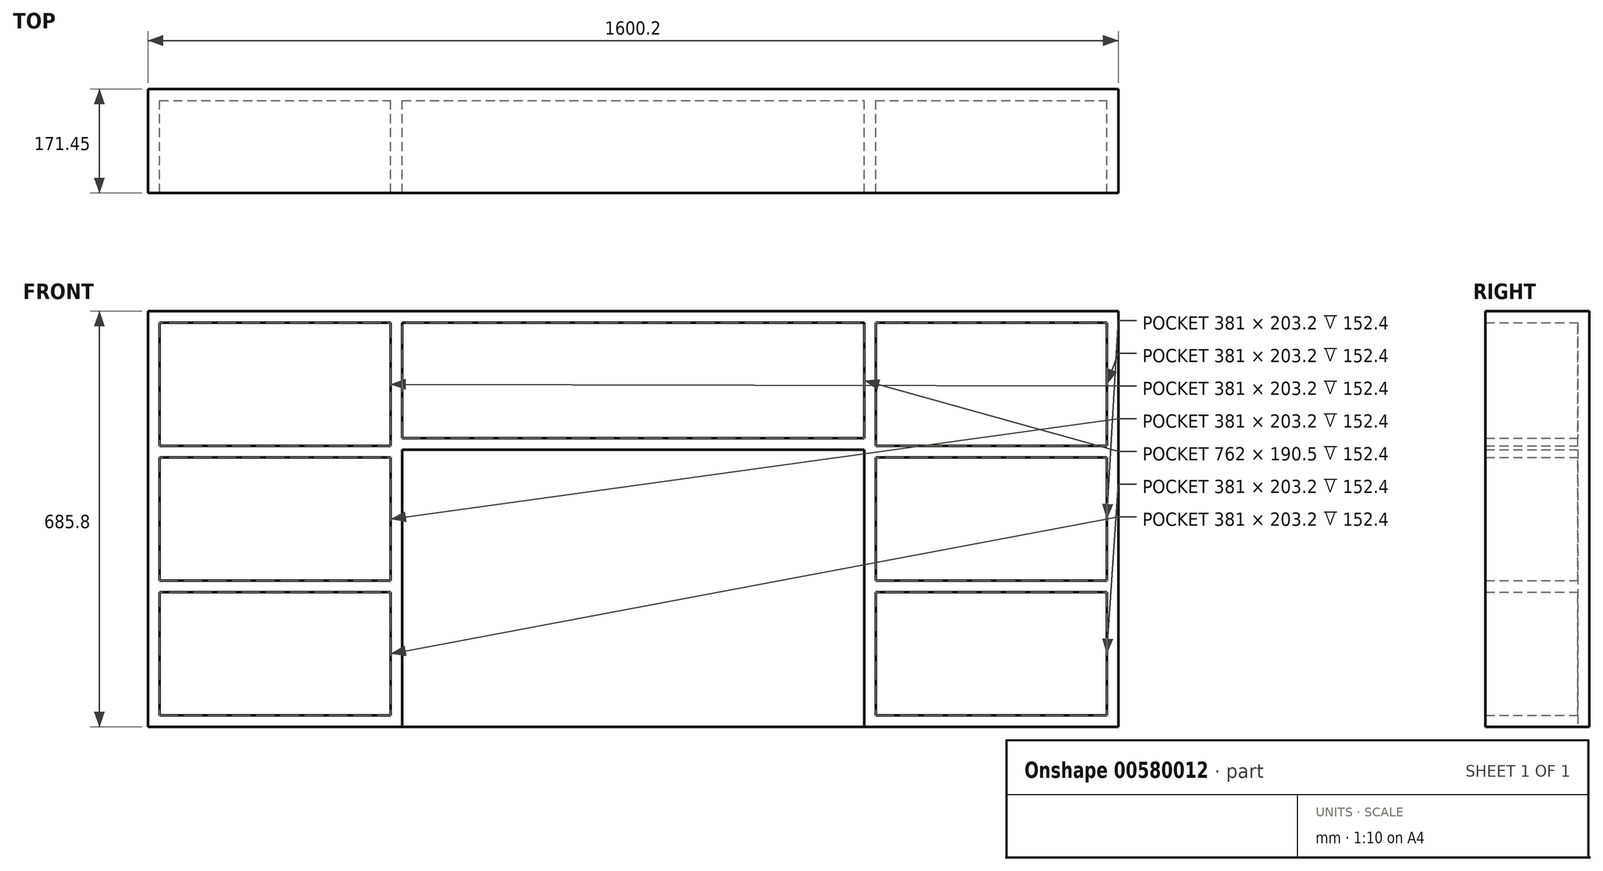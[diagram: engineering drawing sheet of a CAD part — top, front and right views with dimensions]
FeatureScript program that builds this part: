
annotation { "Feature Type Name" : "Feature", "Feature Type Description" : "" }
export const myFeature = defineFeature(function(context is Context, id is Id, definition is map)
    precondition{}
    {
        {
            var Q0;
            Q0=qCreatedBy(makeId("Front.planeOp"),FACE);
            var sketch = newSketch(context, id + "F0", { "sketchPlane" : qUnion([Q0])});
            skLineSegment(sketch, "E0.bottom", {"start": v(0, 0) * mm, "end": v(1600.2, 0) * mm});
            skLineSegment(sketch, "E0.top", {"start": v(0, 685.8) * mm, "end": v(1600.2, 685.8) * mm});
            skLineSegment(sketch, "E0.left", {"start": v(0, 0) * mm, "end": v(0, 685.8) * mm});
            skLineSegment(sketch, "E0.right", {"start": v(1600.2, 0) * mm, "end": v(1600.2, 685.8) * mm});
            skSolve(sketch);
        }
        {
            var Q0;
            Q0=makeQuery(id+"F0.imprint","IMPRINT",FACE,{"disambiguationData":[TD([[makeQuery(id+"F0.imprint","IMPRINT",EDGE,{"derivedFrom":sQuery(id+"F0.wireOp",EDGE,"E0.bottom")}),1.0]])]});
            extrude(context, id + "F1", {"entities" : qUnion([Q0]), "depth" : 19.05 * mm, "offsetDistance" : 25.4 * mm});
        }
        {
            var Q0;
            Q0=makeQuery(id+"F1.opExtrude","CAP_FACE",FACE,{"disambiguationData":[OSD([sQuery(id+"F0.wireOp",EDGE,"E0.bottom"),sQuery(id+"F0.wireOp",EDGE,"E0.top"),sQuery(id+"F0.wireOp",EDGE,"E0.left"),sQuery(id+"F0.wireOp",EDGE,"E0.right")])],"isStart":false});
            var sketch = newSketch(context, id + "F2", { "sketchPlane" : qUnion([Q0])});
            skLineSegment(sketch, "E1", {"start": v(0, 0) * mm, "end": v(19.05, 0) * mm});
            skLineSegment(sketch, "E2", {"start": v(19.05, 0) * mm, "end": v(19.05, 666.75) * mm});
            skLineSegment(sketch, "E3", {"start": v(19.05, 666.75) * mm, "end": v(1581.15, 666.75) * mm});
            skLineSegment(sketch, "E4", {"start": v(1581.15, 666.75) * mm, "end": v(1581.15, 0) * mm});
            skLineSegment(sketch, "E5", {"start": v(1581.15, 0) * mm, "end": v(1600.2, 0) * mm});
            skLineSegment(sketch, "E6", {"start": v(1600.2, 0) * mm, "end": v(1600.2, 685.8) * mm});
            skLineSegment(sketch, "E7", {"start": v(1600.2, 685.8) * mm, "end": v(0, 685.8) * mm});
            skLineSegment(sketch, "E8", {"start": v(0, 685.8) * mm, "end": v(0, 0) * mm});
            skSolve(sketch);
        }
        {
            var Q0;
            Q0=makeQuery(id+"F2.imprint","IMPRINT",FACE,{"disambiguationData":[TD([[makeQuery(id+"F2.imprint","IMPRINT",EDGE,{"derivedFrom":sQuery(id+"F2.wireOp",EDGE,"E1")}),1.0]])]});
            extrude(context, id + "F3", {"entities" : qUnion([Q0]), "operationType" : NewBodyOperationType.ADD, "depth" : 152.4 * mm, "offsetDistance" : 25.4 * mm});
        }
        {
            var Q0;
            Q0=makeQuery(id+"F1.opExtrude","CAP_FACE",FACE,{"disambiguationData":[OSD([sQuery(id+"F0.wireOp",EDGE,"E0.bottom"),sQuery(id+"F0.wireOp",EDGE,"E0.top"),sQuery(id+"F0.wireOp",EDGE,"E0.left"),sQuery(id+"F0.wireOp",EDGE,"E0.right")])],"isStart":false});
            var sketch = newSketch(context, id + "F4", { "sketchPlane" : qUnion([Q0])});
            skLineSegment(sketch, "E9", {"start": v(419.1, 666.75) * mm, "end": v(419.1, 0) * mm});
            skLineSegment(sketch, "E10", {"start": v(419.1, 0) * mm, "end": v(19.05, 0) * mm});
            skLineSegment(sketch, "E11", {"start": v(19.05, 0) * mm, "end": v(19.05, 19.05) * mm});
            skLineSegment(sketch, "E12", {"start": v(19.05, 19.05) * mm, "end": v(400.05, 19.05) * mm});
            skLineSegment(sketch, "E13", {"start": v(400.05, 19.05) * mm, "end": v(400.05, 666.75) * mm});
            skLineSegment(sketch, "E14", {"start": v(400.05, 666.75) * mm, "end": v(419.1, 666.75) * mm});
            skLineSegment(sketch, "E15", {"start": v(800.1, 666.75) * mm, "end": v(800.1, 413.93) * mm, "construction": true});
            skLineSegment(sketch, "E16.MirrorCS", {"start": v(1181.1, 666.75) * mm, "end": v(1181.1, 0) * mm});
            skLineSegment(sketch, "E17.MirrorCS", {"start": v(1200.15, 19.05) * mm, "end": v(1200.15, 666.75) * mm});
            skLineSegment(sketch, "E18.MirrorCS", {"start": v(1581.15, 19.05) * mm, "end": v(1200.15, 19.05) * mm});
            skLineSegment(sketch, "E19.MirrorCS", {"start": v(1181.1, 0) * mm, "end": v(1581.15, 0) * mm});
            skSolve(sketch);
        }
        {
            var Q0;
            Q0=makeQuery(id+"F4.imprint","IMPRINT",FACE,{"disambiguationData":[TD([[makeQuery(id+"F4.imprint","IMPRINT",EDGE,{"derivedFrom":sQuery(id+"F4.wireOp",EDGE,"E9")}),-1.0]])]});
            var Q1;
            {var subQ3=sQuery(id+"F4.wireOp",EDGE,"E16.MirrorCS");Q1=makeQuery(id+"F4.imprint","IMPRINT",FACE,{"disambiguationData":[TD([[makeQuery(id+"F4.imprint","IMPRINT",EDGE,{"derivedFrom":subQ3}),1.0]])]});}
            extrude(context, id + "F5", {"entities" : qUnion([Q0, Q1]), "operationType" : NewBodyOperationType.ADD, "depth" : 152.4 * mm, "offsetDistance" : 25.4 * mm});
        }
        {
            var Q0;
            {var subQ0=sQuery(id+"F0.wireOp",EDGE,"E0.bottom");Q0=makeQuery(id+"F5.boolean.opBoolean","SPLIT",FACE,{"disambiguationData":[TD([makeQuery(id+"F1.opExtrude","SWEPT_FACE",FACE,{"disambiguationData":[OSD([subQ0])]})])],"derivedFrom":makeQuery(id+"F1.opExtrude","CAP_FACE",FACE,{"disambiguationData":[OSD([subQ0,sQuery(id+"F0.wireOp",EDGE,"E0.top"),sQuery(id+"F0.wireOp",EDGE,"E0.left"),sQuery(id+"F0.wireOp",EDGE,"E0.right")])],"isStart":false})});}
            var sketch = newSketch(context, id + "F6", { "sketchPlane" : qUnion([Q0])});
            skLineSegment(sketch, "E20.bottom", {"start": v(419.1, 476.25) * mm, "end": v(1181.1, 476.25) * mm});
            skLineSegment(sketch, "E20.top", {"start": v(419.1, 457.2) * mm, "end": v(1181.1, 457.2) * mm});
            skLineSegment(sketch, "E20.left", {"start": v(419.1, 476.25) * mm, "end": v(419.1, 457.2) * mm});
            skLineSegment(sketch, "E20.right", {"start": v(1181.1, 476.25) * mm, "end": v(1181.1, 457.2) * mm});
            skSolve(sketch);
        }
        {
            var Q0;
            Q0=makeQuery(id+"F6.imprint","IMPRINT",FACE,{"disambiguationData":[TD([[makeQuery(id+"F6.imprint","IMPRINT",EDGE,{"derivedFrom":sQuery(id+"F6.wireOp",EDGE,"E20.bottom")}),-1.0]])]});
            extrude(context, id + "F7", {"entities" : qUnion([Q0]), "operationType" : NewBodyOperationType.ADD, "depth" : 152.4 * mm, "offsetDistance" : 25.4 * mm});
        }
        {
            var Q0;
            Q0=makeQuery(id+"F5.boolean.opBoolean","SPLIT",FACE,{"disambiguationData":[TD([makeQuery(id+"F3.opExtrude","SWEPT_FACE",FACE,{"disambiguationData":[OSD([sQuery(id+"F2.wireOp",EDGE,"E2")])]})])],"derivedFrom":makeQuery(id+"F1.opExtrude","CAP_FACE",FACE,{"disambiguationData":[OSD([sQuery(id+"F0.wireOp",EDGE,"E0.bottom"),sQuery(id+"F0.wireOp",EDGE,"E0.top"),sQuery(id+"F0.wireOp",EDGE,"E0.left"),sQuery(id+"F0.wireOp",EDGE,"E0.right")])],"isStart":false})});
            var sketch = newSketch(context, id + "F8", { "sketchPlane" : qUnion([Q0])});
            skLineSegment(sketch, "E21.bottom", {"start": v(19.05, 241.3) * mm, "end": v(400.05, 241.3) * mm});
            skLineSegment(sketch, "E21.top", {"start": v(19.05, 222.25) * mm, "end": v(400.05, 222.25) * mm});
            skLineSegment(sketch, "E21.left", {"start": v(19.05, 241.3) * mm, "end": v(19.05, 222.25) * mm});
            skLineSegment(sketch, "E21.right", {"start": v(400.05, 241.3) * mm, "end": v(400.05, 222.25) * mm});
            skLineSegment(sketch, "E22.bottom", {"start": v(19.05, 463.55) * mm, "end": v(400.05, 463.55) * mm});
            skLineSegment(sketch, "E22.top", {"start": v(19.05, 444.5) * mm, "end": v(400.05, 444.5) * mm});
            skLineSegment(sketch, "E22.left", {"start": v(19.05, 463.55) * mm, "end": v(19.05, 444.5) * mm});
            skLineSegment(sketch, "E22.right", {"start": v(400.05, 463.55) * mm, "end": v(400.05, 444.5) * mm});
            skSolve(sketch);
        }
        {
            var Q0;
            Q0=makeQuery(id+"F8.imprint","IMPRINT",FACE,{"disambiguationData":[TD([[makeQuery(id+"F8.imprint","IMPRINT",EDGE,{"derivedFrom":sQuery(id+"F8.wireOp",EDGE,"E22.bottom")}),-1.0]])]});
            var Q1;
            Q1=makeQuery(id+"F8.imprint","IMPRINT",FACE,{"disambiguationData":[TD([[makeQuery(id+"F8.imprint","IMPRINT",EDGE,{"derivedFrom":sQuery(id+"F8.wireOp",EDGE,"E21.bottom")}),-1.0]])]});
            extrude(context, id + "F9", {"entities" : qUnion([Q0, Q1]), "operationType" : NewBodyOperationType.ADD, "depth" : 152.4 * mm, "offsetDistance" : 25.4 * mm});
        }
        {
            var Q0;
            Q0=makeQuery(id+"F5.boolean.opBoolean","SPLIT",FACE,{"disambiguationData":[TD([makeQuery(id+"F3.opExtrude","SWEPT_FACE",FACE,{"disambiguationData":[OSD([sQuery(id+"F2.wireOp",EDGE,"E4")])]})])],"derivedFrom":makeQuery(id+"F1.opExtrude","CAP_FACE",FACE,{"disambiguationData":[OSD([sQuery(id+"F0.wireOp",EDGE,"E0.bottom"),sQuery(id+"F0.wireOp",EDGE,"E0.top"),sQuery(id+"F0.wireOp",EDGE,"E0.left"),sQuery(id+"F0.wireOp",EDGE,"E0.right")])],"isStart":false})});
            var sketch = newSketch(context, id + "F10", { "sketchPlane" : qUnion([Q0])});
            skLineSegment(sketch, "E23.bottom", {"start": v(1200.15, 463.55) * mm, "end": v(1581.15, 463.55) * mm});
            skLineSegment(sketch, "E23.top", {"start": v(1200.15, 444.5) * mm, "end": v(1581.15, 444.5) * mm});
            skLineSegment(sketch, "E23.left", {"start": v(1200.15, 463.55) * mm, "end": v(1200.15, 444.5) * mm});
            skLineSegment(sketch, "E23.right", {"start": v(1581.15, 463.55) * mm, "end": v(1581.15, 444.5) * mm});
            skLineSegment(sketch, "E24.bottom", {"start": v(1200.15, 241.3) * mm, "end": v(1581.15, 241.3) * mm});
            skLineSegment(sketch, "E24.top", {"start": v(1200.15, 222.25) * mm, "end": v(1581.15, 222.25) * mm});
            skLineSegment(sketch, "E24.left", {"start": v(1200.15, 241.3) * mm, "end": v(1200.15, 222.25) * mm});
            skLineSegment(sketch, "E24.right", {"start": v(1581.15, 241.3) * mm, "end": v(1581.15, 222.25) * mm});
            skSolve(sketch);
        }
        {
            var Q0;
            Q0=makeQuery(id+"F10.imprint","IMPRINT",FACE,{"disambiguationData":[TD([[makeQuery(id+"F10.imprint","IMPRINT",EDGE,{"derivedFrom":sQuery(id+"F10.wireOp",EDGE,"E23.bottom")}),-1.0]])]});
            var Q1;
            Q1=makeQuery(id+"F10.imprint","IMPRINT",FACE,{"disambiguationData":[TD([[makeQuery(id+"F10.imprint","IMPRINT",EDGE,{"derivedFrom":sQuery(id+"F10.wireOp",EDGE,"E24.bottom")}),-1.0]])]});
            extrude(context, id + "F11", {"entities" : qUnion([Q0, Q1]), "operationType" : NewBodyOperationType.ADD, "depth" : 152.4 * mm, "offsetDistance" : 25.4 * mm});
        }
    });
